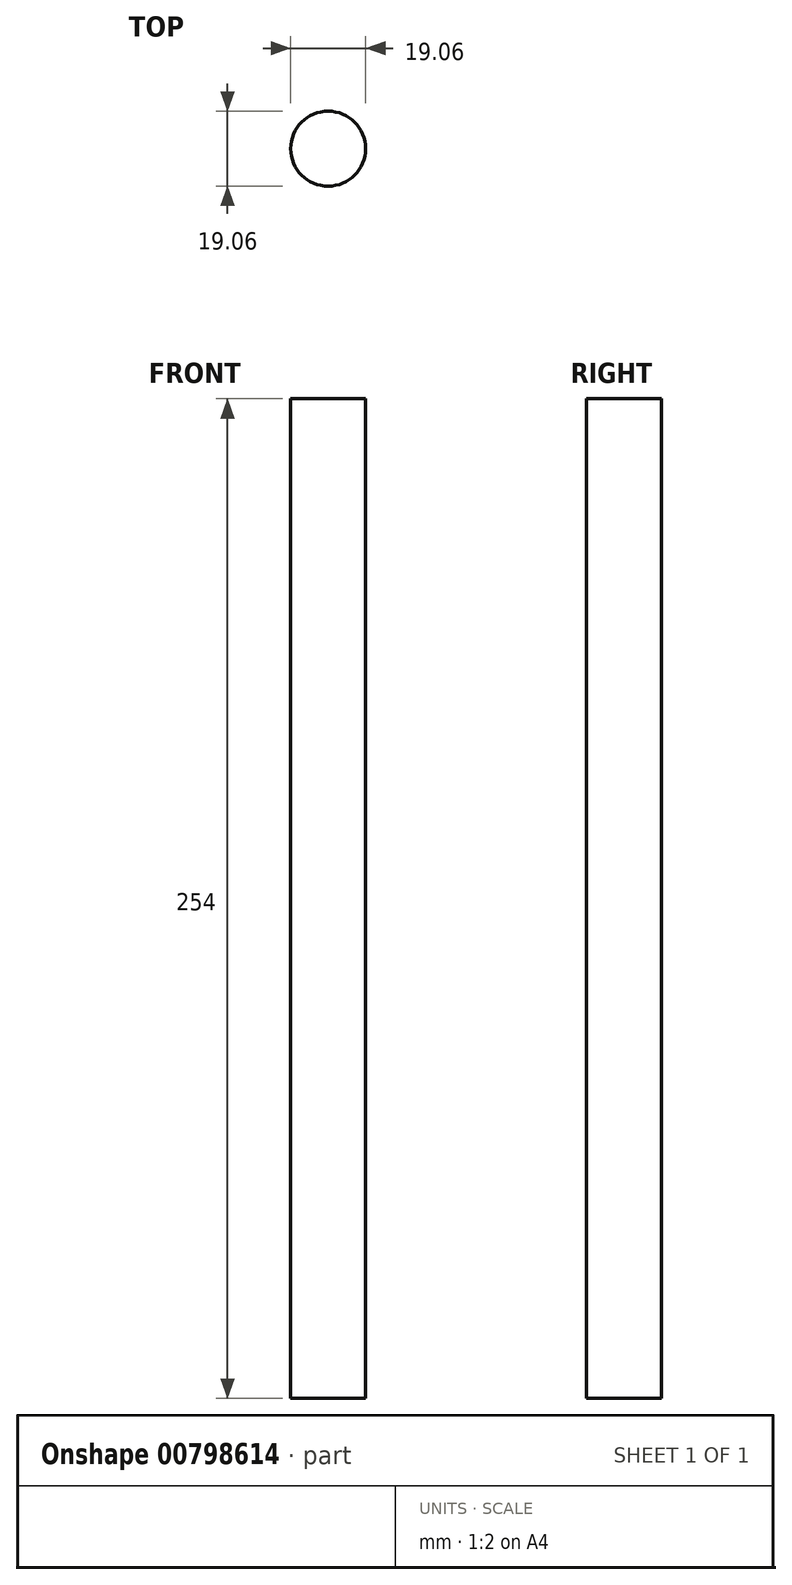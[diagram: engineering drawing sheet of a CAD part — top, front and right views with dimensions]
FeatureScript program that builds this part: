
annotation { "Feature Type Name" : "Feature", "Feature Type Description" : "" }
export const myFeature = defineFeature(function(context is Context, id is Id, definition is map)
    precondition{}
    {
        {
            var Q0;
            Q0=qCreatedBy(makeId("Top.planeOp"),FACE);
            var sketch = newSketch(context, id + "F0", { "sketchPlane" : qUnion([Q0])});
            skCircle(sketch, "E0", {"center": v(0, 0) * mm, "radius": 9.53 * mm});
            skSolve(sketch);
        }
        {
            var Q0;
            Q0=makeQuery(id+"F0.imprint","IMPRINT",FACE,{"disambiguationData":[TD([[makeQuery(id+"F0.imprint","IMPRINT",EDGE,{"derivedFrom":sQuery(id+"F0.wireOp",EDGE,"E0")}),1.0]])]});
            extrude(context, id + "F1", {"entities" : qUnion([Q0]), "depth" : 254 * mm, "offsetDistance" : 25.4 * mm});
        }
    });
